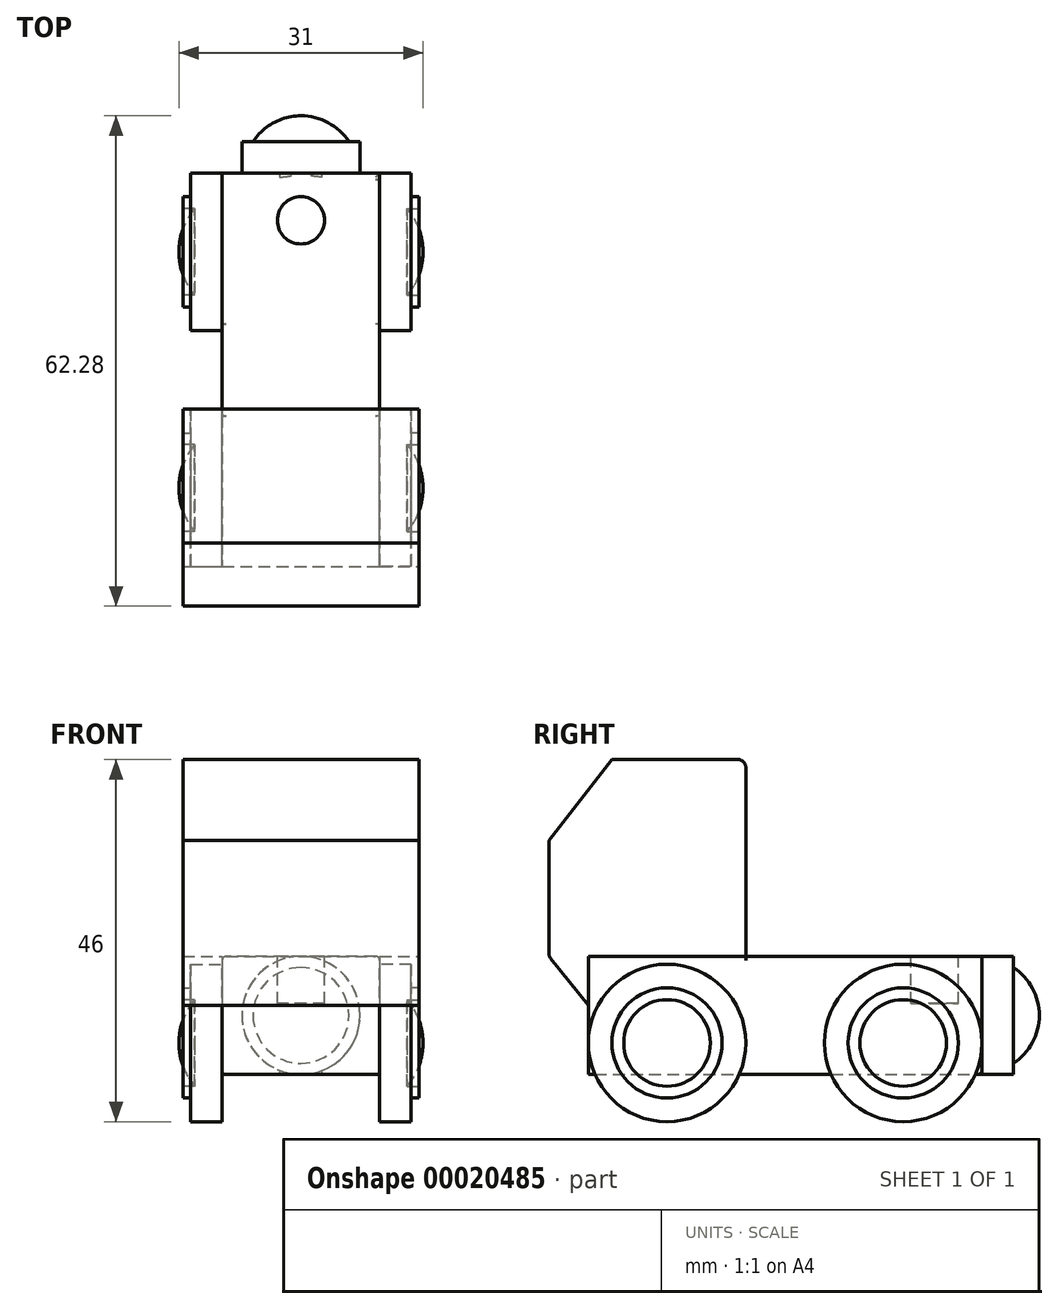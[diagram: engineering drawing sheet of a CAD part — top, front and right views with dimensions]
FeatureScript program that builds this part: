
annotation { "Feature Type Name" : "Feature", "Feature Type Description" : "" }
export const myFeature = defineFeature(function(context is Context, id is Id, definition is map)
    precondition{}
    {
        {
            var Q0;
            Q0=qCreatedBy(makeId("Front.planeOp"),FACE);
            var sketch = newSketch(context, id + "F0", { "sketchPlane" : qUnion([Q0])});
            skLineSegment(sketch, "E0.rect.bottom", {"start": v(-10, 7.5) * mm, "end": v(10, 7.5) * mm});
            skLineSegment(sketch, "E0.rect.top", {"start": v(-10, -7.5) * mm, "end": v(10, -7.5) * mm});
            skLineSegment(sketch, "E0.rect.left", {"start": v(-10, 7.5) * mm, "end": v(-10, -7.5) * mm});
            skLineSegment(sketch, "E0.rect.right", {"start": v(10, 7.5) * mm, "end": v(10, -7.5) * mm});
            skPoint(sketch, "E0.rect.middle", {"position": v(0, 0) * mm});
            skSolve(sketch);
        }
        {
            var Q0;
            Q0 = qSketchRegion(id + "F0", true);
            extrude(context, id + "F1", {"entities" : qUnion([Q0]), "endBound" : BoundingType.SYMMETRIC, "depth" : 50 * mm});
        }
        {
            var Q0;
            Q0=makeQuery(id+"F1.opExtrude","SWEPT_FACE",FACE,{"disambiguationData":[OSD([sQuery(id+"F0.wireOp",EDGE,"E0.rect.bottom")])]});
            var sketch = newSketch(context, id + "F2", { "sketchPlane" : qUnion([Q0])});
            skLineSegment(sketch, "E1.rect.bottom", {"start": v(15, -5) * mm, "end": v(-15, -5) * mm});
            skLineSegment(sketch, "E1.rect.top", {"start": v(15, -30) * mm, "end": v(-15, -30) * mm});
            skLineSegment(sketch, "E1.rect.left", {"start": v(15, -5) * mm, "end": v(15, -30) * mm});
            skLineSegment(sketch, "E1.rect.right", {"start": v(-15, -5) * mm, "end": v(-15, -30) * mm});
            skPoint(sketch, "E1.rect.middle", {"position": v(0, -17.5) * mm});
            skSolve(sketch);
        }
        {
            var Q0;
            Q0 = qSketchRegion(id + "F2", true);
            extrude(context, id + "F3", {"entities" : qUnion([Q0]), "operationType" : NewBodyOperationType.ADD, "depth" : 25 * mm});
        }
        {
            var Q0;
            Q0=makeQuery(id+"F3.opExtrude","SWEPT_FACE",FACE,{"disambiguationData":[OSD([sQuery(id+"F2.wireOp",EDGE,"E1.rect.left")])]});
            var sketch = newSketch(context, id + "F4", { "sketchPlane" : qUnion([Q0])});
            skLineSegment(sketch, "E2.0", {"start": v(-25, 7.5) * mm, "end": v(-25, -7.5) * mm});
            skLineSegment(sketch, "E3", {"start": v(-30, 7.5) * mm, "end": v(-25, 7.5) * mm});
            skLineSegment(sketch, "E4", {"start": v(-25, 1.26) * mm, "end": v(-30, 7.5) * mm});
            skSolve(sketch);
        }
        {
            var Q0;
            Q0 = qSketchRegion(id + "F4", true);
            var Q1;
            Q1=makeQuery(id+"F3.opExtrude","SWEPT_FACE",FACE,{"disambiguationData":[OSD([sQuery(id+"F2.wireOp",EDGE,"E1.rect.right")])]});
            extrude(context, id + "F5", {"entities" : qUnion([Q0]), "operationType" : NewBodyOperationType.ADD, "endBound" : BoundingType.UP_TO_SURFACE, "oppositeDirection" : true, "endBoundEntityFace" : qUnion([Q1]), "depth" : 33.12 * mm});
        }
        {
            var Q0;
            Q0=makeQuery(id+"F5.boolean.opBoolean","MERGE",FACE,{"derivedFrom":[makeQuery(id+"F3.opExtrude","SWEPT_FACE",FACE,{"disambiguationData":[OSD([sQuery(id+"F2.wireOp",EDGE,"E1.rect.left")])]}),makeQuery(id+"F5.opExtrude","CAP_FACE",FACE,{"disambiguationData":[OSD([sQuery(id+"F4.wireOp",EDGE,"E2.0"),sQuery(id+"F4.wireOp",EDGE,"E3"),sQuery(id+"F4.wireOp",EDGE,"E4")])],"isStart":true})]});
            var sketch = newSketch(context, id + "F6", { "sketchPlane" : qUnion([Q0])});
            skLineSegment(sketch, "E5", {"start": v(-30, 32.5) * mm, "end": v(-22, 32.5) * mm});
            skLineSegment(sketch, "E6", {"start": v(-22, 32.5) * mm, "end": v(-30, 22.25) * mm});
            skLineSegment(sketch, "E7", {"start": v(-30, 22.25) * mm, "end": v(-30, 32.5) * mm});
            skSolve(sketch);
        }
        {
            var Q0;
            Q0=makeQuery(id+"F6.imprint","IMPRINT",FACE,{"disambiguationData":[TD([[makeQuery(id+"F6.imprint","IMPRINT",EDGE,{"derivedFrom":sQuery(id+"F6.wireOp",EDGE,"E5")}),1.0]])]});
            var Q1;
            Q1=makeQuery(id+"F5.boolean.opBoolean","MERGE",FACE,{"derivedFrom":[makeQuery(id+"F3.opExtrude","SWEPT_FACE",FACE,{"disambiguationData":[OSD([sQuery(id+"F2.wireOp",EDGE,"E1.rect.right")])]}),makeQuery(id+"F5.opExtrude","CAP_FACE",FACE,{"disambiguationData":[OSD([sQuery(id+"F4.wireOp",EDGE,"E2.0"),sQuery(id+"F4.wireOp",EDGE,"E3"),sQuery(id+"F4.wireOp",EDGE,"E4")])],"isStart":false})]});
            extrude(context, id + "F7", {"entities" : qUnion([Q0]), "operationType" : NewBodyOperationType.REMOVE, "endBound" : BoundingType.UP_TO_SURFACE, "oppositeDirection" : true, "endBoundEntityFace" : qUnion([Q1]), "depth" : 25 * mm});
        }
        {
            var Q0;
            Q0=makeQuery(id+"F1.opExtrude","CAP_FACE",FACE,{"disambiguationData":[OSD([sQuery(id+"F0.wireOp",EDGE,"E0.rect.bottom"),sQuery(id+"F0.wireOp",EDGE,"E0.rect.top"),sQuery(id+"F0.wireOp",EDGE,"E0.rect.left"),sQuery(id+"F0.wireOp",EDGE,"E0.rect.right")])],"isStart":true});
            var sketch = newSketch(context, id + "F8", { "sketchPlane" : qUnion([Q0])});
            skCircle(sketch, "E8", {"center": v(0, 0) * mm, "radius": 7.5 * mm});
            skSolve(sketch);
        }
        {
            var Q0;
            Q0 = qSketchRegion(id + "F8", true);
            extrude(context, id + "F9", {"entities" : qUnion([Q0]), "operationType" : NewBodyOperationType.ADD, "depth" : 4 * mm});
        }
        {
            var Q0;
            Q0=qCreatedBy(makeId("Top.planeOp"),FACE);
            var sketch = newSketch(context, id + "F10", { "sketchPlane" : qUnion([Q0])});
            skLineSegment(sketch, "E9.0", {"start": v(-7.5, 29) * mm, "end": v(7.5, 29) * mm});
            skPoint(sketch, "E10.0", {"position": v(0, 25) * mm});
            skArc(sketch, "E11", {"start": v(0, 32.28) * mm, "mid": v(-3.46, 31.41) * mm, "end": v(-6.09, 29) * mm});
            skPoint(sketch, "E12", {"position": v(0, 32.28) * mm});
            skLineSegment(sketch, "E13", {"start": v(0, 32.28) * mm, "end": v(0, 29) * mm});
            skLineSegment(sketch, "E14", {"start": v(0, 29) * mm, "end": v(-6.09, 29) * mm});
            skSolve(sketch);
        }
        {
            var Q0;
            Q0 = qSketchRegion(id + "F10", true);
            var Q1;
            Q1=sQuery(id+"F10.wireOp",EDGE,"E13");
            revolve(context, id + "F11", {"operationType" : NewBodyOperationType.ADD, "entities" : qUnion([Q0]), "axis" : qUnion([Q1]), "revolveType" : RevolveType.FULL});
        }
        {
            var Q0;
            Q0=makeQuery(id+"F1.opExtrude","SWEPT_FACE",FACE,{"disambiguationData":[OSD([sQuery(id+"F0.wireOp",EDGE,"E0.rect.bottom")])]});
            var sketch = newSketch(context, id + "F12", { "sketchPlane" : qUnion([Q0])});
            skCircle(sketch, "E15", {"center": v(0, 19) * mm, "radius": 3 * mm});
            skSolve(sketch);
        }
        {
            var Q0;
            Q0 = qSketchRegion(id + "F12", true);
            var Q1;
            Q1 = qSketchRegion(id + "FijJH3UXgOABgZZ_1", true);
            extrude(context, id + "F13", {"entities" : qUnion([Q0, Q1]), "operationType" : NewBodyOperationType.REMOVE, "oppositeDirection" : true, "depth" : 6 * mm});
        }
        {
            var Q0;
            Q0=makeQuery(id+"F1.opExtrude","SWEPT_FACE",FACE,{"disambiguationData":[OSD([sQuery(id+"F0.wireOp",EDGE,"E0.rect.left")])]});
            var sketch = newSketch(context, id + "F14", { "sketchPlane" : qUnion([Q0])});
            skCircle(sketch, "E16", {"center": v(15, -3.5) * mm, "radius": 10 * mm});
            skCircle(sketch, "E17", {"center": v(-15, -3.5) * mm, "radius": 10 * mm});
            skSolve(sketch);
        }
        {
            var Q0;
            Q0 = qSketchRegion(id + "F14", true);
            var Q1;
            Q1 = qSketchRegion(id + "F25", true);
            extrude(context, id + "F15", {"entities" : qUnion([Q0, Q1]), "operationType" : NewBodyOperationType.ADD, "depth" : 4 * mm});
        }
        {
            var Q0;
            Q0=makeQuery(id+"F15.opExtrude","CAP_FACE",FACE,{"disambiguationData":[OSD([sQuery(id+"F14.wireOp",EDGE,"E16")])],"isStart":false});
            var sketch = newSketch(context, id + "F16", { "sketchPlane" : qUnion([Q0])});
            skCircle(sketch, "E18", {"center": v(15, -3.5) * mm, "radius": 7 * mm});
            skCircle(sketch, "E19", {"center": v(-15, -3.5) * mm, "radius": 7 * mm});
            skSolve(sketch);
        }
        {
            var Q0;
            Q0 = qSketchRegion(id + "F16", true);
            extrude(context, id + "F17", {"entities" : qUnion([Q0]), "operationType" : NewBodyOperationType.ADD, "depth" : 1 * mm});
        }
        {
            var Q0;
            Q0=makeQuery(id+"F17.opExtrude","CAP_FACE",FACE,{"disambiguationData":[OSD([sQuery(id+"F16.wireOp",EDGE,"E19")])],"isStart":false});
            var sketch = newSketch(context, id + "F18", { "sketchPlane" : qUnion([Q0])});
            skCircle(sketch, "E20", {"center": v(-15, -3.5) * mm, "radius": 5.5 * mm});
            skCircle(sketch, "E21", {"center": v(15, -3.5) * mm, "radius": 5.5 * mm});
            skSolve(sketch);
        }
        {
            var Q0;
            Q0 = qSketchRegion(id + "F18", true);
            extrude(context, id + "F19", {"entities" : qUnion([Q0]), "operationType" : NewBodyOperationType.REMOVE, "oppositeDirection" : true, "depth" : 1.5 * mm});
        }
        {
            var Q0;
            Q0=qCreatedBy(makeId("Top.planeOp"),FACE);
            cPlane(context, id + "F20", {"entities" : qUnion([Q0]), "cplaneType" : CPlaneType.OFFSET, "offset" : 3.5 * mm, "oppositeDirection" : true, "width" : 150 * mm, "height" : 150 * mm});
        }
        {
            var Q0;
            Q0=qCreatedBy(id+"F20.planeOp",FACE);
            var sketch = newSketch(context, id + "F21", { "sketchPlane" : qUnion([Q0])});
            skLineSegment(sketch, "E22.0", {"start": v(-13.5, 9.5) * mm, "end": v(-13.5, 15) * mm});
            skArc(sketch, "E23", {"start": v(-15.5, 15) * mm, "mid": v(-14.98, 12.07) * mm, "end": v(-13.5, 9.5) * mm});
            skLineSegment(sketch, "E24", {"start": v(-15.5, 15) * mm, "end": v(-13.5, 15) * mm});
            skPoint(sketch, "E25.orphan", {"position": v(-13.5, 20.5) * mm});
            skSolve(sketch);
        }
        {
            var Q0;
            Q0 = qSketchRegion(id + "F21", true);
            var Q1;
            Q1=sQuery(id+"F21.wireOp",EDGE,"E24");
            revolve(context, id + "F22", {"operationType" : NewBodyOperationType.ADD, "entities" : qUnion([Q0]), "axis" : qUnion([Q1]), "revolveType" : RevolveType.FULL});
        }
        {
            var Q0;
            Q0=qCreatedBy(id+"F20.planeOp",FACE);
            var sketch = newSketch(context, id + "F23", { "sketchPlane" : qUnion([Q0])});
            skLineSegment(sketch, "E26.0", {"start": v(-13.5, -20.5) * mm, "end": v(-13.5, -15) * mm});
            skArc(sketch, "E27", {"start": v(-15.5, -15) * mm, "mid": v(-14.98, -17.93) * mm, "end": v(-13.5, -20.5) * mm});
            skLineSegment(sketch, "E28", {"start": v(-15.5, -15) * mm, "end": v(-13.5, -15) * mm});
            skPoint(sketch, "E29.orphan", {"position": v(-13.5, -9.5) * mm});
            skSolve(sketch);
        }
        {
            var Q0;
            Q0 = qSketchRegion(id + "F23", true);
            var Q1;
            Q1=sQuery(id+"F23.wireOp",EDGE,"E28");
            revolve(context, id + "F24", {"operationType" : NewBodyOperationType.ADD, "entities" : qUnion([Q0]), "axis" : qUnion([Q1]), "revolveType" : RevolveType.FULL});
        }
        {
            var Q0;
            Q0=makeQuery(id+"F1.opExtrude","SWEPT_FACE",FACE,{"disambiguationData":[OSD([sQuery(id+"F0.wireOp",EDGE,"E0.rect.right")])]});
            var sketch = newSketch(context, id + "F25", { "sketchPlane" : qUnion([Q0])});
            skCircle(sketch, "E30", {"center": v(-15, -3.5) * mm, "radius": 10 * mm});
            skCircle(sketch, "E31", {"center": v(15, -3.5) * mm, "radius": 10 * mm});
            skSolve(sketch);
        }
        {
            var Q0;
            Q0 = qSketchRegion(id + "F25", true);
            extrude(context, id + "F26", {"entities" : qUnion([Q0]), "operationType" : NewBodyOperationType.ADD, "depth" : 4 * mm});
        }
        {
            var Q0;
            Q0=makeQuery(id+"F26.opExtrude","CAP_FACE",FACE,{"disambiguationData":[OSD([sQuery(id+"F25.wireOp",EDGE,"E30")])],"isStart":false});
            var sketch = newSketch(context, id + "F27", { "sketchPlane" : qUnion([Q0])});
            skCircle(sketch, "E32", {"center": v(-15, -3.5) * mm, "radius": 7 * mm});
            skCircle(sketch, "E33", {"center": v(15, -3.5) * mm, "radius": 7 * mm});
            skSolve(sketch);
        }
        {
            var Q0;
            Q0 = qSketchRegion(id + "F27", true);
            extrude(context, id + "F28", {"entities" : qUnion([Q0]), "operationType" : NewBodyOperationType.ADD, "depth" : 1 * mm});
        }
        {
            var Q0;
            Q0=makeQuery(id+"F28.opExtrude","CAP_FACE",FACE,{"disambiguationData":[OSD([sQuery(id+"F27.wireOp",EDGE,"E32")])],"isStart":false});
            var sketch = newSketch(context, id + "F29", { "sketchPlane" : qUnion([Q0])});
            skCircle(sketch, "E34", {"center": v(-15, -3.5) * mm, "radius": 5.5 * mm});
            skCircle(sketch, "E35", {"center": v(15, -3.5) * mm, "radius": 5.5 * mm});
            skSolve(sketch);
        }
        {
            var Q0;
            Q0 = qSketchRegion(id + "F29", true);
            extrude(context, id + "F30", {"entities" : qUnion([Q0]), "operationType" : NewBodyOperationType.REMOVE, "oppositeDirection" : true, "depth" : 1.5 * mm});
        }
        {
            var Q0;
            Q0=qCreatedBy(id+"F20.planeOp",FACE);
            var sketch = newSketch(context, id + "F31", { "sketchPlane" : qUnion([Q0])});
            skLineSegment(sketch, "E36.0", {"start": v(13.5, 20.5) * mm, "end": v(13.5, 9.5) * mm});
            skLineSegment(sketch, "E37.0", {"start": v(13.5, -9.5) * mm, "end": v(13.5, -15) * mm});
            skArc(sketch, "E38", {"start": v(15.5, -15) * mm, "mid": v(14.98, -12.07) * mm, "end": v(13.5, -9.5) * mm});
            skLineSegment(sketch, "E39", {"start": v(13.5, -15) * mm, "end": v(15.5, -15) * mm});
            skPoint(sketch, "E40.orphan", {"position": v(13.5, -20.5) * mm});
            skSolve(sketch);
        }
        {
            var Q0;
            Q0 = qSketchRegion(id + "F31", true);
            var Q1;
            Q1=sQuery(id+"F31.wireOp",EDGE,"E39");
            revolve(context, id + "F32", {"operationType" : NewBodyOperationType.ADD, "entities" : qUnion([Q0]), "axis" : qUnion([Q1]), "revolveType" : RevolveType.FULL});
        }
        {
            var Q0;
            Q0=qCreatedBy(id+"F20.planeOp",FACE);
            var sketch = newSketch(context, id + "F33", { "sketchPlane" : qUnion([Q0])});
            skLineSegment(sketch, "E41.0", {"start": v(13.5, 20.5) * mm, "end": v(13.5, 15) * mm});
            skArc(sketch, "E42", {"start": v(15.5, 15) * mm, "mid": v(14.98, 17.93) * mm, "end": v(13.5, 20.5) * mm});
            skLineSegment(sketch, "E43", {"start": v(13.5, 15) * mm, "end": v(15.5, 15) * mm});
            skPoint(sketch, "E44.orphan", {"position": v(13.5, 9.5) * mm});
            skSolve(sketch);
        }
        {
            var Q0;
            Q0 = qSketchRegion(id + "F33", true);
            var Q1;
            Q1=sQuery(id+"F33.wireOp",EDGE,"E43");
            revolve(context, id + "F34", {"operationType" : NewBodyOperationType.ADD, "entities" : qUnion([Q0]), "axis" : qUnion([Q1]), "revolveType" : RevolveType.FULL});
        }
        {
            var Q0;
            {var subQ0=sQuery(id+"F0.wireOp",EDGE,"E0.rect.bottom");var subQ1=sQuery(id+"F0.wireOp",EDGE,"E0.rect.right");Q0=makeQuery(id+"F3.boolean.opBoolean","SPLIT",EDGE,{"disambiguationData":[TD([makeQuery(id+"F1.opExtrude","CAP_FACE",FACE,{"disambiguationData":[OSD([subQ0,sQuery(id+"F0.wireOp",EDGE,"E0.rect.top"),sQuery(id+"F0.wireOp",EDGE,"E0.rect.left"),subQ1])],"isStart":true})])],"derivedFrom":makeQuery(id+"F1.opExtrude","SWEPT_EDGE",EDGE,{"disambiguationData":[OSD([subQ0,subQ1])]})});}
            var Q1;
            {var subQ0=sQuery(id+"F0.wireOp",EDGE,"E0.rect.bottom");var subQ1=sQuery(id+"F0.wireOp",EDGE,"E0.rect.left");Q1=makeQuery(id+"F3.boolean.opBoolean","SPLIT",EDGE,{"disambiguationData":[TD([makeQuery(id+"F1.opExtrude","CAP_FACE",FACE,{"disambiguationData":[OSD([subQ0,sQuery(id+"F0.wireOp",EDGE,"E0.rect.top"),subQ1,sQuery(id+"F0.wireOp",EDGE,"E0.rect.right")])],"isStart":true})])],"derivedFrom":makeQuery(id+"F1.opExtrude","SWEPT_EDGE",EDGE,{"disambiguationData":[OSD([subQ0,subQ1])]})});}
            var Q2;
            {var subQ0=sQuery(id+"F0.wireOp",EDGE,"E0.rect.top");var subQ1=sQuery(id+"F0.wireOp",EDGE,"E0.rect.left");var subQ2=sQuery(id+"F14.wireOp",EDGE,"E17");var subQ3=sQuery(id+"F14.wireOp",EDGE,"E16");Q2=makeQuery(id+"F15.boolean.opBoolean","SPLIT",EDGE,{"disambiguationData":[TD([makeQuery(id+"F1.opExtrude","SWEPT_FACE",FACE,{"disambiguationData":[OSD([subQ0])]}),makeQuery(id+"F1.opExtrude","SWEPT_FACE",FACE,{"disambiguationData":[OSD([subQ1])]}),makeQuery(id+"F15.opExtrude","SWEPT_FACE",FACE,{"disambiguationData":[OSD([subQ3])]}),makeQuery(id+"F15.opExtrude","CAP_FACE",FACE,{"disambiguationData":[OSD([subQ3])],"isStart":true}),makeQuery(id+"F15.opExtrude","SWEPT_FACE",FACE,{"disambiguationData":[OSD([subQ2])]}),makeQuery(id+"F15.opExtrude","CAP_FACE",FACE,{"disambiguationData":[OSD([subQ2])],"isStart":true})])],"derivedFrom":makeQuery(id+"F1.opExtrude","SWEPT_EDGE",EDGE,{"disambiguationData":[OSD([subQ0,subQ1])]})});}
            var Q3;
            {var subQ0=sQuery(id+"F0.wireOp",EDGE,"E0.rect.top");var subQ1=sQuery(id+"F0.wireOp",EDGE,"E0.rect.right");var subQ2=sQuery(id+"F25.wireOp",EDGE,"E31");var subQ3=sQuery(id+"F25.wireOp",EDGE,"E30");Q3=makeQuery(id+"F26.boolean.opBoolean","SPLIT",EDGE,{"disambiguationData":[TD([makeQuery(id+"F1.opExtrude","SWEPT_FACE",FACE,{"disambiguationData":[OSD([subQ0])]}),makeQuery(id+"F1.opExtrude","SWEPT_FACE",FACE,{"disambiguationData":[OSD([subQ1])]}),makeQuery(id+"F26.opExtrude","SWEPT_FACE",FACE,{"disambiguationData":[OSD([subQ3])]}),makeQuery(id+"F26.opExtrude","CAP_FACE",FACE,{"disambiguationData":[OSD([subQ3])],"isStart":true}),makeQuery(id+"F26.opExtrude","SWEPT_FACE",FACE,{"disambiguationData":[OSD([subQ2])]}),makeQuery(id+"F26.opExtrude","CAP_FACE",FACE,{"disambiguationData":[OSD([subQ2])],"isStart":true})])],"derivedFrom":makeQuery(id+"F1.opExtrude","SWEPT_EDGE",EDGE,{"disambiguationData":[OSD([subQ0,subQ1])]})});}
            var Q4;
            {var subQ0=sQuery(id+"F0.wireOp",EDGE,"E0.rect.top");var subQ1=sQuery(id+"F0.wireOp",EDGE,"E0.rect.right");Q4=makeQuery(id+"F9.boolean.opBoolean","SPLIT",EDGE,{"disambiguationData":[TD([makeQuery(id+"F1.opExtrude","SWEPT_FACE",FACE,{"disambiguationData":[OSD([subQ1])]})])],"derivedFrom":makeQuery(id+"F1.opExtrude","CAP_EDGE",EDGE,{"disambiguationData":[OSD([subQ0])],"isStart":true})});}
            var Q5;
            {var subQ0=sQuery(id+"F0.wireOp",EDGE,"E0.rect.top");var subQ1=sQuery(id+"F0.wireOp",EDGE,"E0.rect.right");var subQ2=sQuery(id+"F25.wireOp",EDGE,"E31");Q5=makeQuery(id+"F26.boolean.opBoolean","SPLIT",EDGE,{"disambiguationData":[TD([makeQuery(id+"F1.opExtrude","CAP_FACE",FACE,{"disambiguationData":[OSD([sQuery(id+"F0.wireOp",EDGE,"E0.rect.bottom"),subQ0,sQuery(id+"F0.wireOp",EDGE,"E0.rect.left"),subQ1])],"isStart":true}),makeQuery(id+"F1.opExtrude","SWEPT_FACE",FACE,{"disambiguationData":[OSD([subQ0])]}),makeQuery(id+"F1.opExtrude","SWEPT_FACE",FACE,{"disambiguationData":[OSD([subQ1])]}),makeQuery(id+"F26.opExtrude","SWEPT_FACE",FACE,{"disambiguationData":[OSD([subQ2])]}),makeQuery(id+"F26.opExtrude","CAP_FACE",FACE,{"disambiguationData":[OSD([subQ2])],"isStart":true})])],"derivedFrom":makeQuery(id+"F1.opExtrude","SWEPT_EDGE",EDGE,{"disambiguationData":[OSD([subQ0,subQ1])]})});}
            fillet(context, id + "F35", {"entities" : qUnion([Q0, Q1, Q2, Q3, Q4, Q5]), "radius" : 0.5 * mm, "tangentPropagation" : true, "allowEdgeOverflow" : false});
        }
        {
            var Q0;
            Q0=makeQuery(id+"F7.boolean.opBoolean","COPY",EDGE,{"derivedFrom":makeQuery(id+"F7.opExtrude","SWEPT_EDGE",EDGE,{"disambiguationData":[OSD([sQuery(id+"F2.wireOp",EDGE,"E1.rect.left"),sQuery(id+"F6.wireOp",EDGE,"E5"),sQuery(id+"F6.wireOp",EDGE,"E6")])]})});
            var Q1;
            Q1=makeQuery(id+"F7.boolean.opBoolean","COPY",EDGE,{"derivedFrom":makeQuery(id+"F7.opExtrude","SWEPT_EDGE",EDGE,{"disambiguationData":[OSD([sQuery(id+"F2.wireOp",EDGE,"E1.rect.top"),sQuery(id+"F2.wireOp",EDGE,"E1.rect.left"),sQuery(id+"F6.wireOp",EDGE,"E6"),sQuery(id+"F6.wireOp",EDGE,"E7")])]})});
            var Q2;
            {var subQ0=sQuery(id+"F2.wireOp",EDGE,"E1.rect.top");Q2=makeQuery(id+"F5.boolean.opBoolean","MERGE",EDGE,{"derivedFrom":[makeQuery(id+"F3.opExtrude","CAP_EDGE",EDGE,{"disambiguationData":[OSD([subQ0])],"isStart":true}),makeQuery(id+"F5.opExtrude","SWEPT_EDGE",EDGE,{"disambiguationData":[OSD([subQ0,sQuery(id+"F2.wireOp",EDGE,"E1.rect.left"),sQuery(id+"F4.wireOp",EDGE,"E3"),sQuery(id+"F4.wireOp",EDGE,"E4")])]})]});}
            var Q3;
            Q3=makeQuery(id+"F3.opExtrude","CAP_EDGE",EDGE,{"disambiguationData":[OSD([sQuery(id+"F2.wireOp",EDGE,"E1.rect.bottom")])],"isStart":false});
            fillet(context, id + "F36", {"entities" : qUnion([Q0, Q1, Q2, Q3]), "radius" : 1 * mm, "tangentPropagation" : true, "allowEdgeOverflow" : false});
        }
    });
